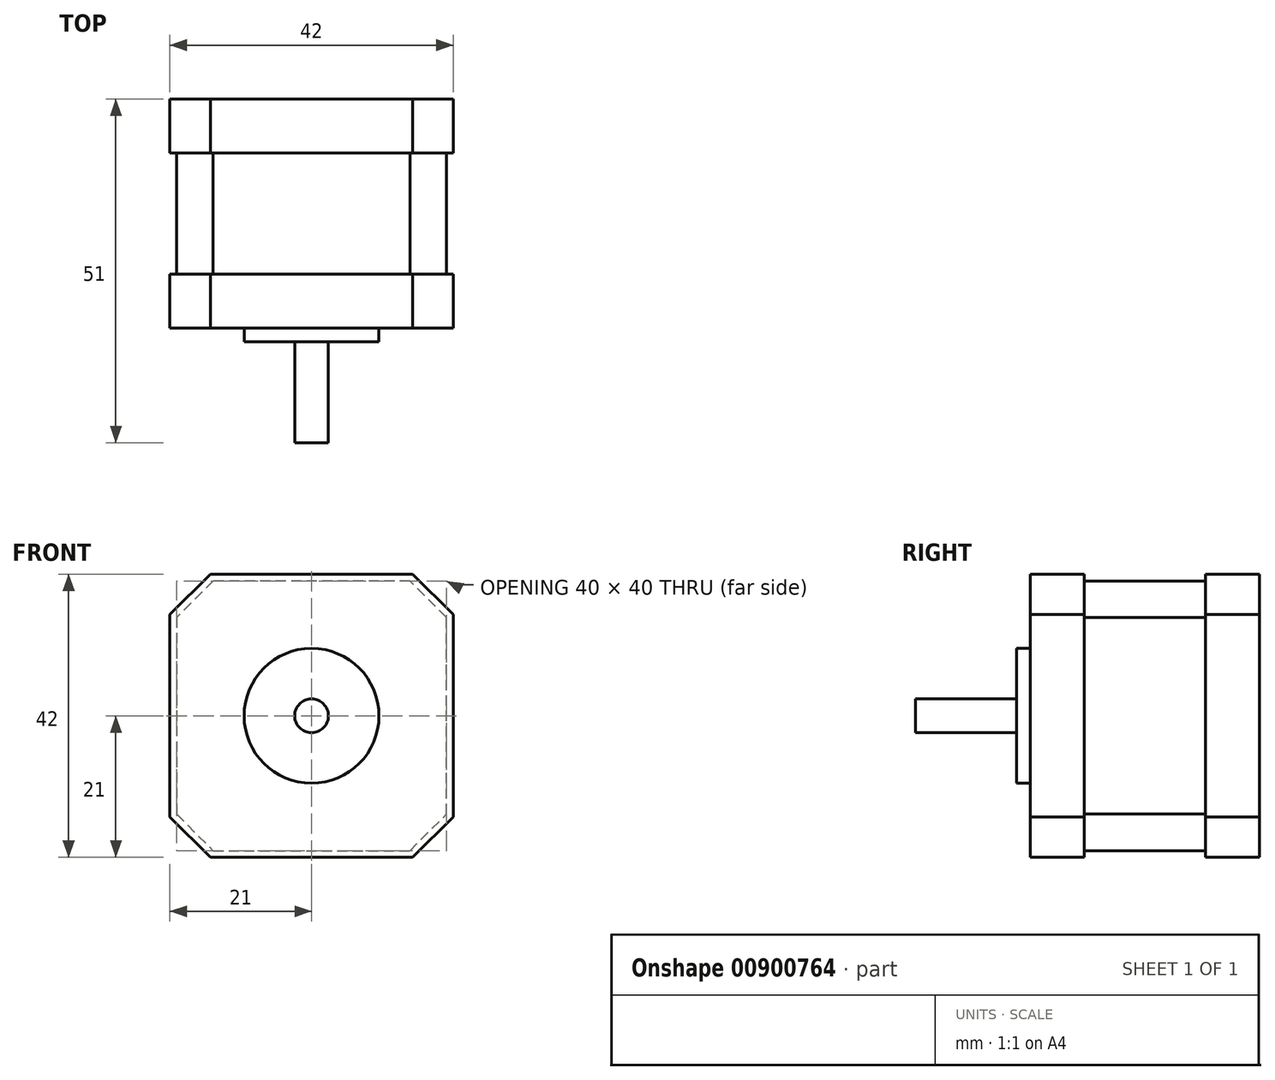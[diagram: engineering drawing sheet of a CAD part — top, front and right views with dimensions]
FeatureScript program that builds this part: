
annotation { "Feature Type Name" : "Feature", "Feature Type Description" : "" }
export const myFeature = defineFeature(function(context is Context, id is Id, definition is map)
    precondition{}
    {
        {
            var Q0;
            Q0=qCreatedBy(makeId("Front.planeOp"),FACE);
            var sketch = newSketch(context, id + "F0", { "sketchPlane" : qUnion([Q0])});
            skLineSegment(sketch, "E0.bottom", {"start": v(-21, -21) * mm, "end": v(21, -21) * mm});
            skLineSegment(sketch, "E0.top", {"start": v(-21, 21) * mm, "end": v(21, 21) * mm});
            skLineSegment(sketch, "E0.left", {"start": v(-21, -21) * mm, "end": v(-21, 21) * mm});
            skLineSegment(sketch, "E0.right", {"start": v(21, -21) * mm, "end": v(21, 21) * mm});
            skLineSegment(sketch, "E1", {"start": v(-21, 21) * mm, "end": v(21, -21) * mm, "construction": true});
            skSolve(sketch);
        }
        {
            var Q0;
            Q0 = qSketchRegion(id + "F0", true);
            extrude(context, id + "F1", {"entities" : qUnion([Q0]), "oppositeDirection" : true, "depth" : 34 * mm, "offsetDistance" : 25 * mm});
        }
        {
            var Q0;
            Q0=makeQuery(id+"F1.opExtrude","SWEPT_EDGE",EDGE,{"disambiguationData":[OSD([sQuery(id+"F0.wireOp",EDGE,"E0.top"),sQuery(id+"F0.wireOp",EDGE,"E0.right")])]});
            var Q1;
            Q1=makeQuery(id+"F1.opExtrude","SWEPT_EDGE",EDGE,{"disambiguationData":[OSD([sQuery(id+"F0.wireOp",EDGE,"E0.top"),sQuery(id+"F0.wireOp",EDGE,"E0.left")])]});
            var Q2;
            Q2=makeQuery(id+"F1.opExtrude","SWEPT_EDGE",EDGE,{"disambiguationData":[OSD([sQuery(id+"F0.wireOp",EDGE,"E0.bottom"),sQuery(id+"F0.wireOp",EDGE,"E0.right")])]});
            var Q3;
            Q3=makeQuery(id+"F1.opExtrude","SWEPT_EDGE",EDGE,{"disambiguationData":[OSD([sQuery(id+"F0.wireOp",EDGE,"E0.bottom"),sQuery(id+"F0.wireOp",EDGE,"E0.left")])]});
            chamfer(context, id + "F2", {"entities" : qUnion([Q0, Q1, Q2, Q3]), "width" : 6 * mm, "tangentPropagation" : true});
        }
        {
            var Q0;
            Q0=makeQuery(id+"F1.opExtrude","CAP_FACE",FACE,{"disambiguationData":[OSD([sQuery(id+"F0.wireOp",EDGE,"E0.bottom"),sQuery(id+"F0.wireOp",EDGE,"E0.top"),sQuery(id+"F0.wireOp",EDGE,"E0.left"),sQuery(id+"F0.wireOp",EDGE,"E0.right")])],"isStart":true});
            cPlane(context, id + "F3", {"entities" : qUnion([Q0]), "cplaneType" : CPlaneType.OFFSET, "offset" : 8 * mm, "oppositeDirection" : true, "width" : 150 * mm, "height" : 150 * mm});
        }
        {
            var Q0;
            Q0=qCreatedBy(id+"F3.planeOp",FACE);
            var sketch = newSketch(context, id + "F4", { "sketchPlane" : qUnion([Q0])});
            skLineSegment(sketch, "E2.0", {"start": v(-14.59, 20) * mm, "end": v(-20, 14.59) * mm});
            skLineSegment(sketch, "E2.1", {"start": v(14.59, 20) * mm, "end": v(-14.59, 20) * mm});
            skLineSegment(sketch, "E2.2", {"start": v(-20, 14.59) * mm, "end": v(-20, -14.59) * mm});
            skLineSegment(sketch, "E2.3", {"start": v(20, 14.59) * mm, "end": v(14.59, 20) * mm});
            skLineSegment(sketch, "E2.4", {"start": v(-20, -14.59) * mm, "end": v(-14.59, -20) * mm});
            skLineSegment(sketch, "E2.5", {"start": v(-14.59, -20) * mm, "end": v(14.59, -20) * mm});
            skLineSegment(sketch, "E2.6", {"start": v(14.59, -20) * mm, "end": v(20, -14.59) * mm});
            skLineSegment(sketch, "E2.7", {"start": v(20, -14.59) * mm, "end": v(20, 14.59) * mm});
            skLineSegment(sketch, "E3.0", {"start": v(-15, 21) * mm, "end": v(-21, 15) * mm});
            skLineSegment(sketch, "E4.0.0", {"start": v(-21, 15) * mm, "end": v(-21, -15) * mm});
            skLineSegment(sketch, "E4.0.1", {"start": v(-21, -15) * mm, "end": v(-15, -21) * mm});
            skLineSegment(sketch, "E4.0.2", {"start": v(-15, -21) * mm, "end": v(15, -21) * mm});
            skLineSegment(sketch, "E4.0.3", {"start": v(15, -21) * mm, "end": v(21, -15) * mm});
            skLineSegment(sketch, "E4.0.4", {"start": v(21, -15) * mm, "end": v(21, 15) * mm});
            skLineSegment(sketch, "E4.0.5", {"start": v(21, 15) * mm, "end": v(15, 21) * mm});
            skLineSegment(sketch, "E4.0.6", {"start": v(15, 21) * mm, "end": v(-15, 21) * mm});
            skSolve(sketch);
        }
        {
            var Q0;
            Q0 = qSketchRegion(id + "F4", true);
            extrude(context, id + "F5", {"entities" : qUnion([Q0]), "operationType" : NewBodyOperationType.REMOVE, "oppositeDirection" : true, "depth" : (34 - 16) * mm, "offsetDistance" : 25 * mm});
        }
        {
            var Q0;
            Q0=qCreatedBy(makeId("Front.planeOp"),FACE);
            var sketch = newSketch(context, id + "F6", { "sketchPlane" : qUnion([Q0])});
            skCircle(sketch, "E5", {"center": v(0, 0) * mm, "radius": 10 * mm});
            skSolve(sketch);
        }
        {
            var Q0;
            Q0 = qSketchRegion(id + "F6", true);
            extrude(context, id + "F7", {"entities" : qUnion([Q0]), "operationType" : NewBodyOperationType.ADD, "depth" : 2 * mm, "offsetDistance" : 25 * mm});
        }
        {
            var Q0;
            Q0=makeQuery(id+"F7.opExtrude","CAP_FACE",FACE,{"disambiguationData":[OSD([sQuery(id+"F6.wireOp",EDGE,"E5")])],"isStart":false});
            var sketch = newSketch(context, id + "F8", { "sketchPlane" : qUnion([Q0])});
            skCircle(sketch, "E6", {"center": v(0, 0) * mm, "radius": 2.5 * mm});
            skSolve(sketch);
        }
        {
            var Q0;
            Q0 = qSketchRegion(id + "F8", true);
            extrude(context, id + "F9", {"entities" : qUnion([Q0]), "operationType" : NewBodyOperationType.ADD, "depth" : 15 * mm, "offsetDistance" : 25 * mm});
        }
    });
